# Revit family: HARMANN - VENTIN VL HID STHY2
name_source: partatom
category: Akcesoria wentylacyjne
units: mm (PartAtom-declared; Revit-internal decimal feet)

## family parameters
Obiekt nadrzędny = Powierzchnia
Tnij formami wycięć po wczytaniu = Tak
Typ części = Łączy się z
Współdzielony = Nie
Wymiar okrągłego złącza = Użyj średnicy

## types (1)
- VENTIN VL HID STHY2
    Domyślna rzędna = 1219 mm
    Izolacyjność akustyczna nawiewnik otwarty D n,e,w (C, Ctr) = 58 (-2;-6) dB
    Izolacyjność akustyczna nawiewnik przymkniety D n,e,w (C, Ctr) = 59 (-2;-6) dB
    Kierunek przepływu = Przepły powietrza z zewnętrz do pomieszczenia
    Max Flow = 35.9 m³/h
    Min Flow = 7.3 m³/h
    Model = VENTIN VL HID STHY2
    Montaż = Nawiewniki VENTIN VL HID STHY2 przeznaczone są do montażu z puszką glifową  w ścianach z izolacją termiczną po stronie zewnętrznej budynków mieszkalnych, zamieszkania zbiorowego i użyteczności publicznej.
    Numer artykułu = 04251200
    Opis = Nawiewniki ścienne higrosterowane, akustyczne, z dodatkowym wytłumieniem,  glifowe VENTIN VL HID STHY2
    Producent = Harmann Polska Sp. z o.o.
    URL = https://harmann.pl
    Wydajność nawiewnika otwartego (dP=10Pa) = 26.1 m³/h
    Wydajność nawiewnika otwartego (dP=20Pa) = 35.9 m³/h
    Wydajność nawiewnika przymkniętego (dP=10Pa) = 7.3 m³/h
    Wydajność nawiewnika przymkniętego (dP=20Pa) = 10.5 m³/h
    Zastosowanie = Głównym zastosowaniem jest doprowadzenie powietrza kompensacyjnego do mieszkań, w systemowych rozwiązaniach mechanicznej wentylacji wywiewnej- SENSOVENT. Może być również wykorzystany w pomieszczeniach z wentylacją grawitacyjną, lub hybrydową. Nawiewniki ścienne można stosować w pomieszczeniach przeznaczonych na stały lub czasowy pobyt ludzi w budynkach mieszkalnych, zamieszkania zbiorowego, użyteczności publicznej, biurowych a także produkcyjnych i magazynowych.

## geometry (parser evidence)
native form markers: Sweep x4
no freeform markers — native parametric forms only
